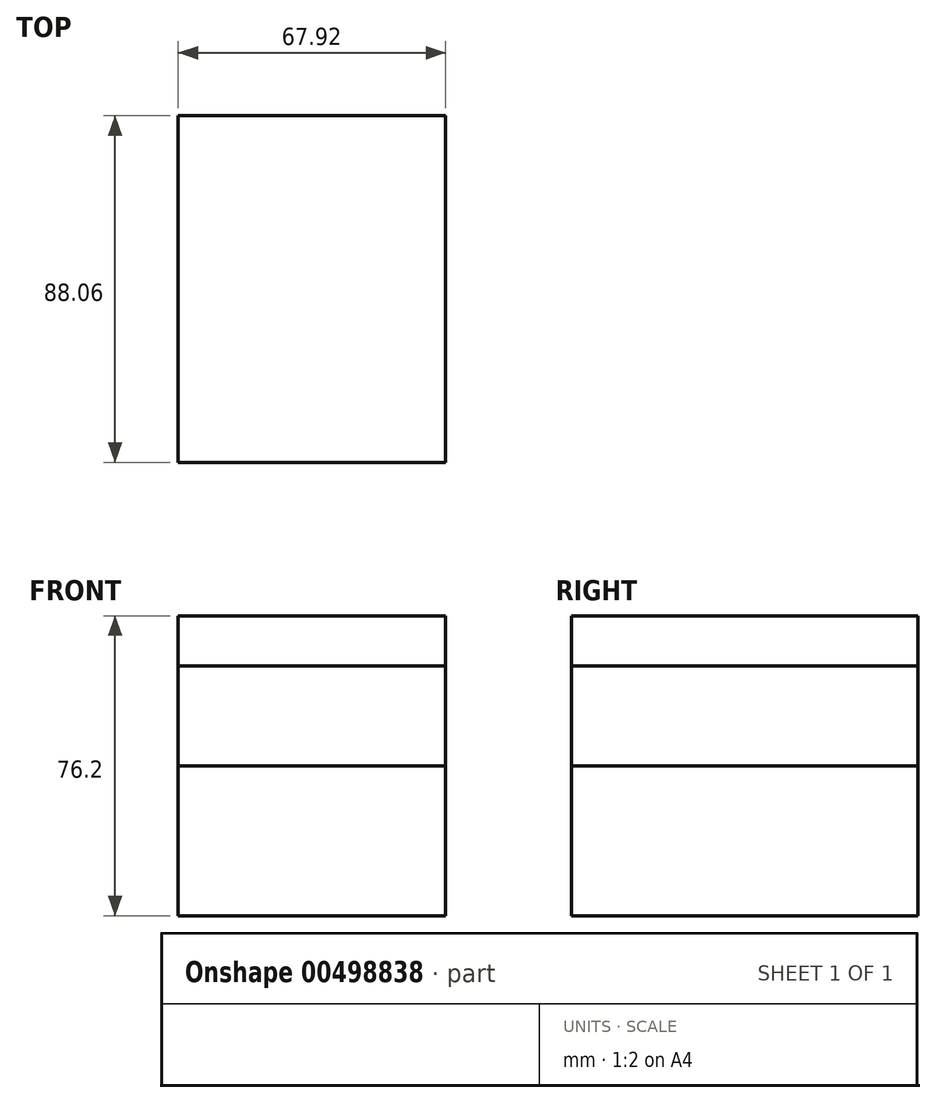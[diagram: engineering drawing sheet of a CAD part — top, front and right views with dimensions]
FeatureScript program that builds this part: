
annotation { "Feature Type Name" : "Feature", "Feature Type Description" : "" }
export const myFeature = defineFeature(function(context is Context, id is Id, definition is map)
    precondition{}
    {
        {
            var Q0;
            Q0=qCreatedBy(makeId("Top.planeOp"),FACE);
            var sketch = newSketch(context, id + "F0", { "sketchPlane" : qUnion([Q0])});
            skLineSegment(sketch, "E0.bottom", {"start": v(33.96, 44.03) * mm, "end": v(-33.96, 44.03) * mm});
            skLineSegment(sketch, "E0.top", {"start": v(33.96, -44.03) * mm, "end": v(-33.96, -44.03) * mm});
            skLineSegment(sketch, "E0.left", {"start": v(33.96, 44.03) * mm, "end": v(33.96, -44.03) * mm});
            skLineSegment(sketch, "E0.right", {"start": v(-33.96, 44.03) * mm, "end": v(-33.96, -44.03) * mm});
            skPoint(sketch, "E0.middle", {"position": v(0, 0) * mm});
            skSolve(sketch);
        }
        {
            var Q0;
            Q0=makeQuery(id+"F0.imprint","IMPRINT",FACE,{"disambiguationData":[TD([[makeQuery(id+"F0.imprint","IMPRINT",EDGE,{"derivedFrom":sQuery(id+"F0.wireOp",EDGE,"E0.bottom")}),1.0]])]});
            extrude(context, id + "F1", {"entities" : qUnion([Q0]), "endBound" : BoundingType.SYMMETRIC, "depth" : 76.2 * mm});
        }
        {
            var Q0;
            Q0=makeQuery(id+"F0.imprint","IMPRINT",FACE,{"disambiguationData":[TD([[makeQuery(id+"F0.imprint","IMPRINT",EDGE,{"derivedFrom":sQuery(id+"F0.wireOp",EDGE,"E0.bottom")}),1.0]])]});
            extrude(context, id + "F2", {"entities" : qUnion([Q0]), "depth" : 25.4 * mm});
        }
    });
